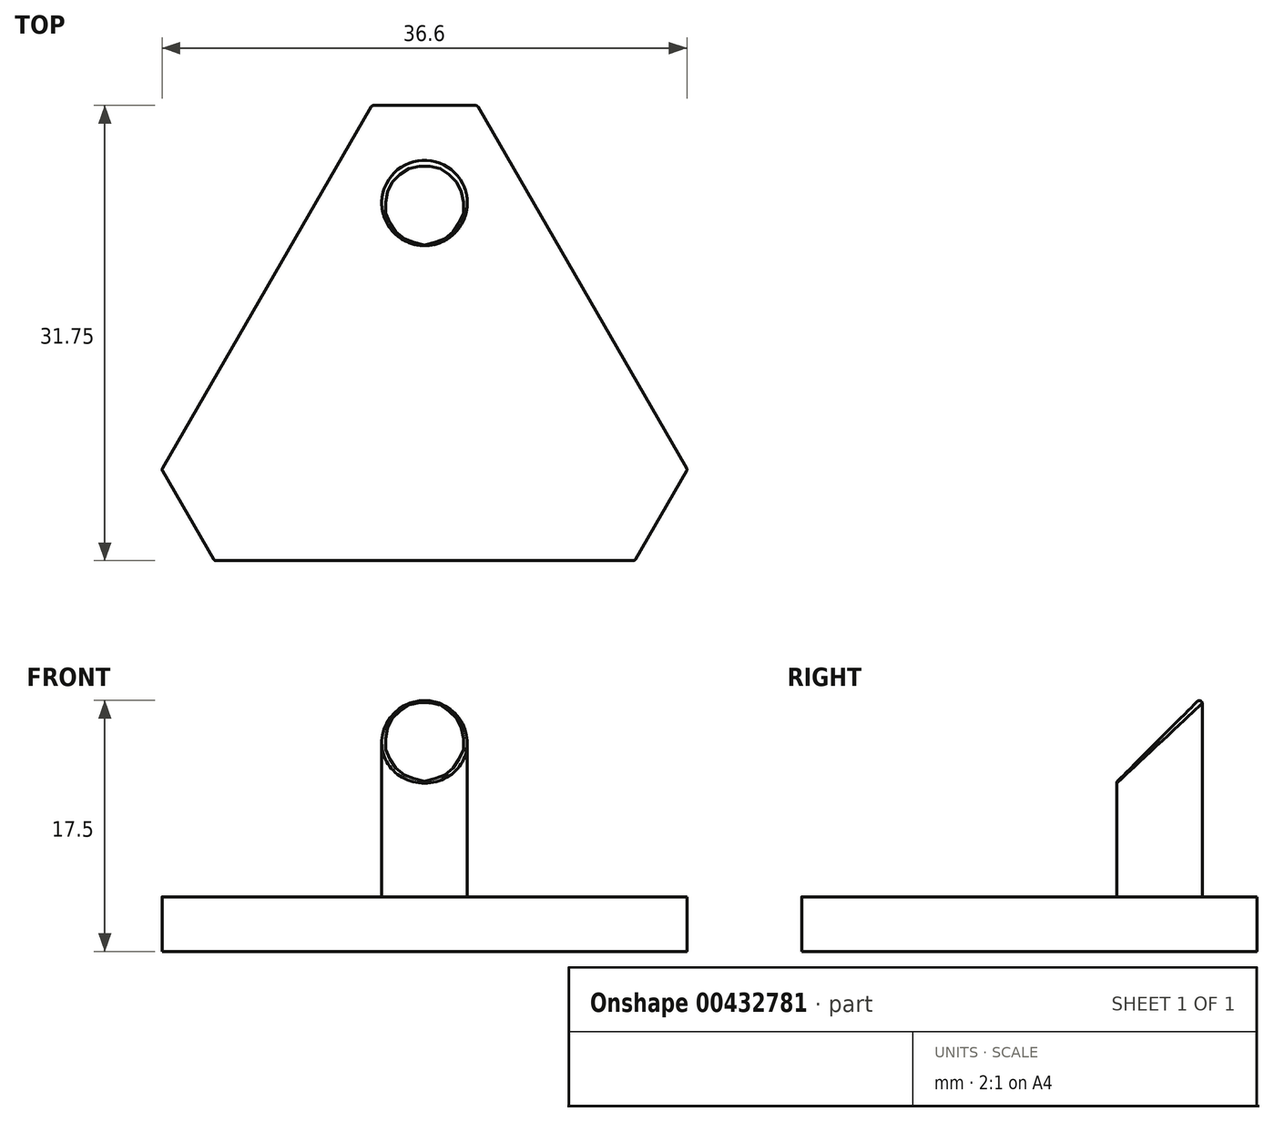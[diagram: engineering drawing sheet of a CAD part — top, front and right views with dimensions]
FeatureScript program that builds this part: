
annotation { "Feature Type Name" : "Feature", "Feature Type Description" : "" }
export const myFeature = defineFeature(function(context is Context, id is Id, definition is map)
    precondition{}
    {
        {
            var Q0;
            Q0=qCreatedBy(makeId("Top.planeOp"),FACE);
            var sketch = newSketch(context, id + "F0", { "sketchPlane" : qUnion([Q0])});
            skPoint(sketch, "E0.middle", {"position": v(0, 0) * mm});
            skLineSegment(sketch, "E1", {"start": v(0, -12.7) * mm, "end": v(0, 25.4) * mm, "construction": true});
            skLineSegment(sketch, "E2", {"start": v(-3.67, 19.05) * mm, "end": v(-18.33, -6.35) * mm});
            skLineSegment(sketch, "E3", {"start": v(-14.66, -12.7) * mm, "end": v(14.66, -12.7) * mm});
            skLineSegment(sketch, "E4", {"start": v(18.33, -6.35) * mm, "end": v(3.67, 19.05) * mm});
            skLineSegment(sketch, "E5", {"start": v(11, 6.35) * mm, "end": v(-22, -12.7) * mm, "construction": true});
            skLineSegment(sketch, "E6", {"start": v(-11, 6.35) * mm, "end": v(22, -12.7) * mm, "construction": true});
            skLineSegment(sketch, "E7.bottom", {"start": v(3.67, 19.05) * mm, "end": v(-3.67, 19.05) * mm});
            skLineSegment(sketch, "E8.1.0", {"start": v(-18.33, -6.35) * mm, "end": v(-14.66, -12.7) * mm});
            skLineSegment(sketch, "E8.2.0", {"start": v(14.66, -12.7) * mm, "end": v(18.33, -6.35) * mm});
            skSolve(sketch);
        }
        {
            var Q0;
            Q0 = qSketchRegion(id + "F0", true);
            extrude(context, id + "F1", {"entities" : qUnion([Q0]), "depth" : 3.8 * mm});
        }
        {
            var Q0;
            Q0=makeQuery(id+"F1.opExtrude","CAP_FACE",FACE,{"disambiguationData":[OSD([sQuery(id+"F0.wireOp",EDGE,"E2"),sQuery(id+"F0.wireOp",EDGE,"E3"),sQuery(id+"F0.wireOp",EDGE,"E4"),sQuery(id+"F0.wireOp",EDGE,"E7.bottom"),sQuery(id+"F0.wireOp",EDGE,"E8.1.0"),sQuery(id+"F0.wireOp",EDGE,"E8.2.0")])],"isStart":false});
            var sketch = newSketch(context, id + "F2", { "sketchPlane" : qUnion([Q0])});
            skCircle(sketch, "E9", {"center": v(0, 12.26) * mm, "radius": 2.98 * mm});
            skSolve(sketch);
        }
        {
            var Q0;
            Q0 = qSketchRegion(id + "F2", true);
            extrude(context, id + "F3", {"entities" : qUnion([Q0]), "operationType" : NewBodyOperationType.ADD, "depth" : 13.97 * mm});
        }
        {
            var Q0;
            Q0=qCreatedBy(makeId("Right.planeOp"),FACE);
            var sketch = newSketch(context, id + "F4", { "sketchPlane" : qUnion([Q0])});
            skLineSegment(sketch, "E10", {"start": v(15.24, 17.78) * mm, "end": v(9.27, 17.78) * mm});
            skLineSegment(sketch, "E11", {"start": v(9.27, 17.78) * mm, "end": v(9.27, 11.81) * mm});
            skLineSegment(sketch, "E12", {"start": v(9.27, 11.81) * mm, "end": v(15.24, 17.78) * mm});
            skSolve(sketch);
        }
        {
            var Q0;
            Q0 = qSketchRegion(id + "F4", true);
            extrude(context, id + "F5", {"entities" : qUnion([Q0]), "operationType" : NewBodyOperationType.REMOVE, "endBound" : BoundingType.SYMMETRIC, "oppositeDirection" : true, "depth" : 25.4 * mm});
        }
        {
            var Q0;
            Q0=qCreatedBy(makeId("Right.planeOp"),FACE);
            var sketch = newSketch(context, id + "F6", { "sketchPlane" : qUnion([Q0])});
            skLineSegment(sketch, "E13", {"start": v(0, 0) * mm, "end": v(0, 38.65) * mm});
            skSolve(sketch);
        }
        {
            var Q0;
            Q0=makeQuery(id+"F1.opExtrude","SWEPT_EDGE",EDGE,{"disambiguationData":[OSD([sQuery(id+"F0.wireOp",EDGE,"E3"),sQuery(id+"F0.wireOp",EDGE,"E8.1.0")])]});
            var Q1;
            Q1=makeQuery(id+"F1.opExtrude","SWEPT_EDGE",EDGE,{"disambiguationData":[OSD([sQuery(id+"F0.wireOp",EDGE,"E3"),sQuery(id+"F0.wireOp",EDGE,"E8.2.0")])]});
            var Q2;
            Q2=makeQuery(id+"F1.opExtrude","SWEPT_EDGE",EDGE,{"disambiguationData":[OSD([sQuery(id+"F0.wireOp",EDGE,"E4"),sQuery(id+"F0.wireOp",EDGE,"E8.2.0")])]});
            var Q3;
            Q3=makeQuery(id+"F1.opExtrude","SWEPT_EDGE",EDGE,{"disambiguationData":[OSD([sQuery(id+"F0.wireOp",EDGE,"E2"),sQuery(id+"F0.wireOp",EDGE,"E8.1.0")])]});
            var Q4;
            Q4=makeQuery(id+"F1.opExtrude","SWEPT_EDGE",EDGE,{"disambiguationData":[OSD([sQuery(id+"F0.wireOp",EDGE,"E2"),sQuery(id+"F0.wireOp",EDGE,"E7.bottom")])]});
            var Q5;
            Q5=makeQuery(id+"F1.opExtrude","SWEPT_EDGE",EDGE,{"disambiguationData":[OSD([sQuery(id+"F0.wireOp",EDGE,"E4"),sQuery(id+"F0.wireOp",EDGE,"E7.bottom")])]});
            var Q6;
            Q6=makeQuery(id+"FqILoXrhuRuEd5K_1.2.F5.boolean.opBoolean","COPY",FACE,{"derivedFrom":makeQuery(id+"FqILoXrhuRuEd5K_1.2.F5.opExtrude","SWEPT_FACE",FACE,{"disambiguationData":[OSD([sQuery(id+"F4.wireOp",EDGE,"E12")])]})});
            var Q7;
            Q7=makeQuery(id+"FqILoXrhuRuEd5K_1.1.F5.boolean.opBoolean","COPY",FACE,{"derivedFrom":makeQuery(id+"FqILoXrhuRuEd5K_1.1.F5.opExtrude","SWEPT_FACE",FACE,{"disambiguationData":[OSD([sQuery(id+"F4.wireOp",EDGE,"E12")])]})});
            var Q8;
            Q8=makeQuery(id+"F5.boolean.opBoolean","COPY",FACE,{"derivedFrom":makeQuery(id+"F5.opExtrude","SWEPT_FACE",FACE,{"disambiguationData":[OSD([sQuery(id+"F4.wireOp",EDGE,"E12")])]})});
            fillet(context, id + "F7", {"entities" : qUnion([Q0, Q1, Q2, Q3, Q4, Q5, Q6, Q7, Q8]), "radius" : .2 * mm, "tangentPropagation" : true, "allowEdgeOverflow" : false});
        }
    });
